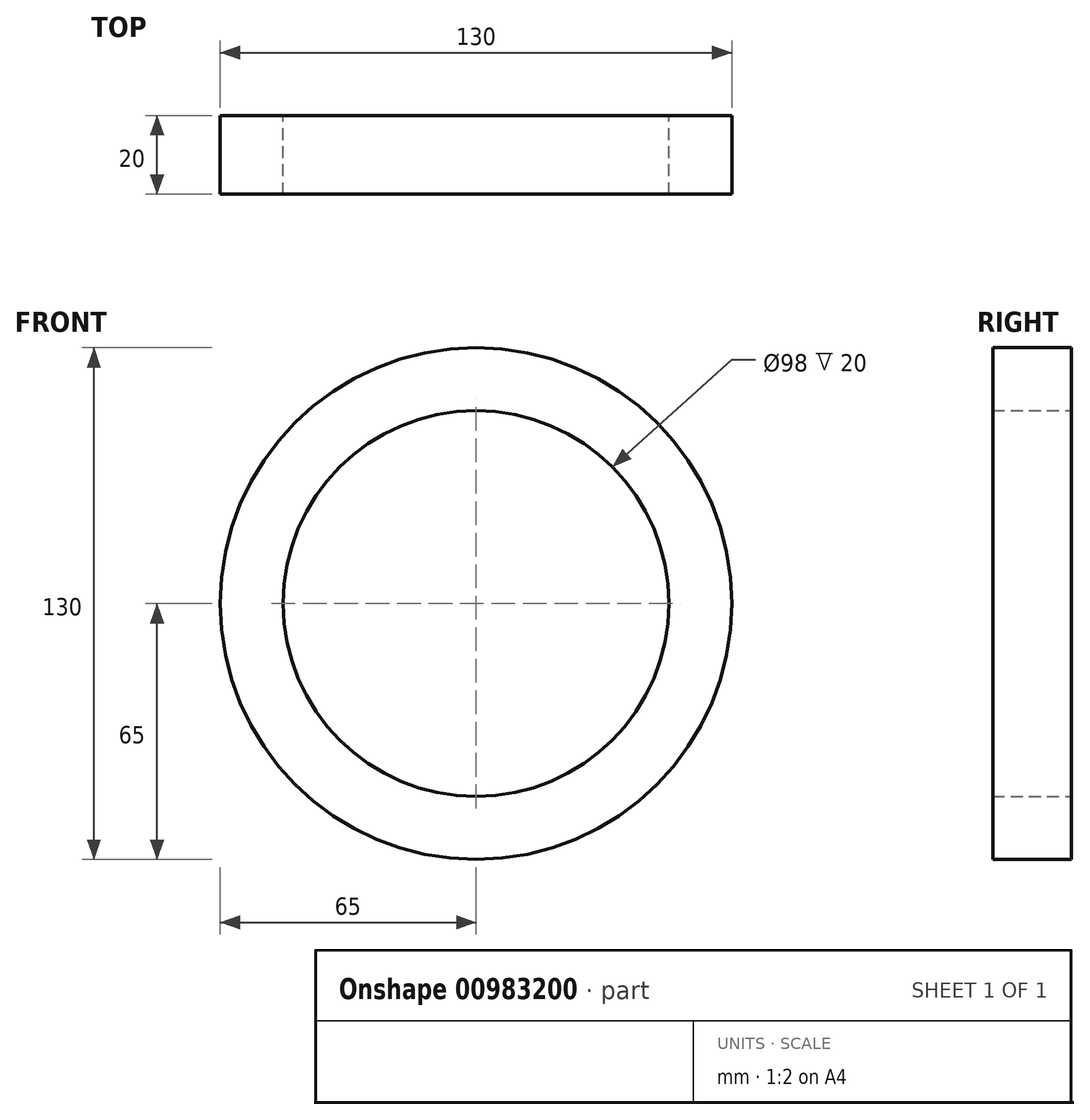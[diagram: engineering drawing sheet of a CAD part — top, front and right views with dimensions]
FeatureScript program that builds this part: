
annotation { "Feature Type Name" : "Feature", "Feature Type Description" : "" }
export const myFeature = defineFeature(function(context is Context, id is Id, definition is map)
    precondition{}
    {
        {
            var Q0;
            Q0=qCreatedBy(makeId("Front.planeOp"),FACE);
            var sketch = newSketch(context, id + "F0", { "sketchPlane" : qUnion([Q0])});
            skCircle(sketch, "E0", {"center": v(0, 0) * mm, "radius": 49 * mm});
            skCircle(sketch, "E1", {"center": v(0, 0) * mm, "radius": 65 * mm});
            skSolve(sketch);
        }
        {
            var Q0;
            Q0=makeQuery(id+"F0.imprint","IMPRINT",FACE,{"disambiguationData":[TD([[makeQuery(id+"F0.imprint","IMPRINT",EDGE,{"derivedFrom":sQuery(id+"F0.wireOp",EDGE,"E0")}),-1.0]])]});
            extrude(context, id + "F1", {"entities" : qUnion([Q0]), "depth" : 20 * mm, "offsetDistance" : 25 * mm});
        }
    });
